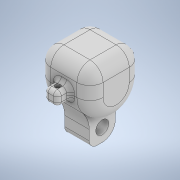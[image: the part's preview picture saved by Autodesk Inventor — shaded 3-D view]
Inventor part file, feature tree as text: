
AUTODESK INVENTOR PART (.ipt)
format: ipt  version: 2022 (Build 260153000, 153)  size: 348,672 bytes
history: native  units: mm
features: fillet x9, extrude x5, sketch x5
ambient origin geometry x8: Origin, YZ Plane, XZ Plane, XY Plane, X Axis, Y Axis, Z Axis, Center Point
bodies: Solide1 (feature_tree)
feature tree (19):
  extrude  "Extrusion1"  Depth=20.0mm
  extrude  "Extrusion2"  Depth=20.0mm
  extrude  "Extrusion3"  Depth=20.0mm TaperAngle=0.0deg
  fillet  "Congé1"  Radius=10.0mm
  fillet  "Congé2"  Radius=10.0mm
  fillet  "Congé5"  Radius=20.0mm
  fillet  "Congé6"  Radius=5.0mm
  fillet  "Congé7"  Radius=20.0mm
  fillet  "Congé9"  Radius=5.0mm
  fillet  "Congé10"  Radius=10.0mm
  extrude  "Extrusion6"  Depth=5.0mm
  extrude  "Extrusion7"  Depth=5.0mm
  fillet  "Congé11"  Radius=5.0mm
  fillet  "Congé12"  Radius=10.0mm
  sketch  "Esquisse1"
  sketch  "Esquisse3"
  sketch  "Esquisse4"
  sketch  "Esquisse10"
  sketch  "Esquisse11"
